# Revit family: Floor_Hatch-Recessed-Cendrex-(PPA-RE)
name_source: partatom
category: Specialty Equipment
revit_build: Autodesk Revit Architecture 2013 (Build: 20130531_2115(x64)
units: mm (PartAtom-declared; Revit-internal decimal feet)

## types (3) — shared parameters
Assembly Code = C1020700
Available Options = http://cendrex.com
Cendrex LEED Ready Program = http://www.cendrex.com
Construction Material = Metal - Cendrex - Aluminum
Default Elevation = 0"
Description = Recessed aluminum floor hatch
Door Width = 24"
Finish = Metal - Cendrex - Powder Coated White
Frame Depth = 1 3/4"
Manufacturer = Cendrex
Model = PPA-RE
Product Documentation Link = http://cendrex.com
Product Page URL = http://cendrex.com
URL = http://www.cendrex.com
Width Actual = 28"
Width Calc = 24"

## per-type parameters (varying)
| type | Door Height | Height Actual | Height Calc |
| Custom | 24" | 28" | 24" |
| 24x24 | 24" | 28" | 24" |
| 24x36 | 36" | 40" | 36" |

## geometry (parser evidence)
native form markers: Blend x22, Sweep x12
no freeform markers — native parametric forms only
